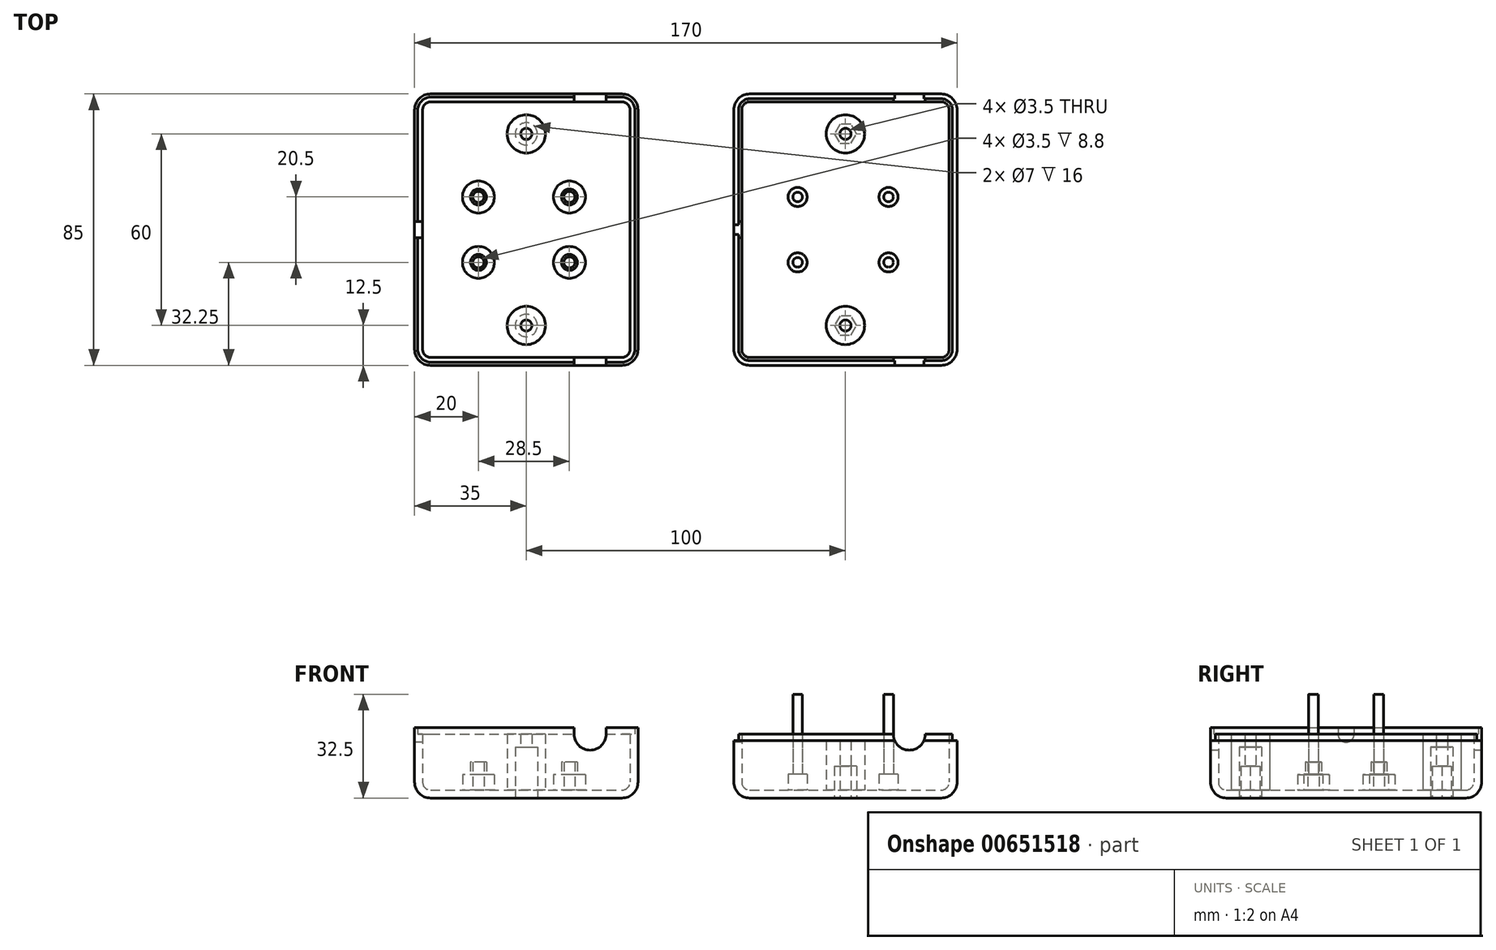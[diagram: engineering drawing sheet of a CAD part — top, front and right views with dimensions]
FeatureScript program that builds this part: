
annotation { "Feature Type Name" : "Feature", "Feature Type Description" : "" }
export const myFeature = defineFeature(function(context is Context, id is Id, definition is map)
    precondition{}
    {
        {
            var Q0;
            Q0=qCreatedBy(makeId("Top.planeOp"),FACE);
            var sketch = newSketch(context, id + "F0", { "sketchPlane" : qUnion([Q0])});
            skLineSegment(sketch, "E0.bottom", {"start": v(0, 0) * mm, "end": v(70, 0) * mm});
            skLineSegment(sketch, "E0.top", {"start": v(0, 85) * mm, "end": v(70, 85) * mm});
            skLineSegment(sketch, "E0.left", {"start": v(0, 0) * mm, "end": v(0, 85) * mm});
            skLineSegment(sketch, "E0.right", {"start": v(70, 0) * mm, "end": v(70, 85) * mm});
            skSolve(sketch);
        }
        {
            var Q0;
            Q0 = qSketchRegion(id + "F0", true);
            extrude(context, id + "F1", {"entities" : qUnion([Q0]), "oppositeDirection" : true, "depth" : 20 * mm, "offsetDistance" : 25 * mm});
        }
        {
            var Q0;
            Q0=makeQuery(id+"F1.opExtrude","CAP_EDGE",EDGE,{"disambiguationData":[OSD([sQuery(id+"F0.wireOp",EDGE,"E0.left")])],"isStart":false});
            var Q1;
            Q1=makeQuery(id+"F1.opExtrude","CAP_FACE",FACE,{"disambiguationData":[OSD([sQuery(id+"F0.wireOp",EDGE,"E0.bottom"),sQuery(id+"F0.wireOp",EDGE,"E0.top"),sQuery(id+"F0.wireOp",EDGE,"E0.left"),sQuery(id+"F0.wireOp",EDGE,"E0.right")])],"isStart":false});
            var Q2;
            Q2=makeQuery(id+"F1.opExtrude","SWEPT_EDGE",EDGE,{"disambiguationData":[OSD([sQuery(id+"F0.wireOp",EDGE,"E0.bottom"),sQuery(id+"F0.wireOp",EDGE,"E0.right")])]});
            var Q3;
            Q3=makeQuery(id+"F1.opExtrude","SWEPT_EDGE",EDGE,{"disambiguationData":[OSD([sQuery(id+"F0.wireOp",EDGE,"E0.bottom"),sQuery(id+"F0.wireOp",EDGE,"E0.left")])]});
            var Q4;
            Q4=makeQuery(id+"F1.opExtrude","SWEPT_EDGE",EDGE,{"disambiguationData":[OSD([sQuery(id+"F0.wireOp",EDGE,"E0.top"),sQuery(id+"F0.wireOp",EDGE,"E0.left")])]});
            var Q5;
            Q5=makeQuery(id+"F1.opExtrude","SWEPT_EDGE",EDGE,{"disambiguationData":[OSD([sQuery(id+"F0.wireOp",EDGE,"E0.top"),sQuery(id+"F0.wireOp",EDGE,"E0.right")])]});
            fillet(context, id + "F2", {"entities" : qUnion([Q0, Q1, Q2, Q3, Q4, Q5]), "radius" : 5 * mm, "tangentPropagation" : true, "allowEdgeOverflow" : false});
        }
        {
            var Q0;
            Q0=makeQuery(id+"F1.opExtrude","CAP_FACE",FACE,{"disambiguationData":[OSD([sQuery(id+"F0.wireOp",EDGE,"E0.bottom"),sQuery(id+"F0.wireOp",EDGE,"E0.top"),sQuery(id+"F0.wireOp",EDGE,"E0.left"),sQuery(id+"F0.wireOp",EDGE,"E0.right")])],"isStart":true});
            shell(context, id + "F3", {"entities" : qUnion([Q0]), "thickness" : 2.5 * mm});
        }
        {
            var Q0;
            Q0=makeQuery(id+"F1.opExtrude","SWEPT_FACE",FACE,{"disambiguationData":[OSD([sQuery(id+"F0.wireOp",EDGE,"E0.left")])]});
            var sketch = newSketch(context, id + "F4", { "sketchPlane" : qUnion([Q0])});
            skCircle(sketch, "E1", {"center": v(-42.5, 0) * mm, "radius": 2.5 * mm});
            skSolve(sketch);
        }
        {
            var Q0;
            Q0 = qSketchRegion(id + "F4", true);
            extrude(context, id + "F5", {"entities" : qUnion([Q0]), "operationType" : NewBodyOperationType.REMOVE, "endBound" : BoundingType.UP_TO_NEXT, "oppositeDirection" : true, "depth" : 25 * mm, "offsetDistance" : 25 * mm});
        }
        {
            var Q0;
            Q0=makeQuery(id+"F1.opExtrude","SWEPT_FACE",FACE,{"disambiguationData":[OSD([sQuery(id+"F0.wireOp",EDGE,"E0.bottom")])]});
            var sketch = newSketch(context, id + "F6", { "sketchPlane" : qUnion([Q0])});
            skCircle(sketch, "E2", {"center": v(55, 0) * mm, "radius": 5 * mm});
            skSolve(sketch);
        }
        {
            var Q0;
            Q0 = qSketchRegion(id + "F6", true);
            extrude(context, id + "F7", {"entities" : qUnion([Q0]), "operationType" : NewBodyOperationType.REMOVE, "endBound" : BoundingType.THROUGH_ALL, "oppositeDirection" : true, "depth" : 25 * mm, "offsetDistance" : 25 * mm});
        }
        {
            var Q0;
            Q0=makeQuery(id+"F3.opShell","OFFSET_FACE",FACE,{"disambiguationData":[OSD([sQuery(id+"F0.wireOp",EDGE,"E0.bottom"),sQuery(id+"F0.wireOp",EDGE,"E0.top"),sQuery(id+"F0.wireOp",EDGE,"E0.left"),sQuery(id+"F0.wireOp",EDGE,"E0.right")])]});
            var sketch = newSketch(context, id + "F8", { "sketchPlane" : qUnion([Q0])});
            skLineSegment(sketch, "E3", {"start": v(5, 42.5) * mm, "end": v(65, 42.5) * mm, "construction": true});
            skLineSegment(sketch, "E4", {"start": v(35, 80) * mm, "end": v(35, 5) * mm, "construction": true});
            skLineSegment(sketch, "E5.bottom", {"start": v(20, 52.75) * mm, "end": v(48.5, 52.75) * mm, "construction": true});
            skLineSegment(sketch, "E5.top", {"start": v(20, 32.25) * mm, "end": v(48.5, 32.25) * mm, "construction": true});
            skLineSegment(sketch, "E5.left", {"start": v(20, 52.75) * mm, "end": v(20, 32.25) * mm, "construction": true});
            skLineSegment(sketch, "E5.right", {"start": v(48.5, 52.75) * mm, "end": v(48.5, 32.25) * mm, "construction": true});
            skSolve(sketch);
        }
        {
            var Q0;
            Q0=makeQuery(id+"F1.opExtrude","SWEPT_BODY",BODY,{"disambiguationData":[OSD([sQuery(id+"F0.wireOp",EDGE,"E0.bottom"),sQuery(id+"F0.wireOp",EDGE,"E0.top"),sQuery(id+"F0.wireOp",EDGE,"E0.left"),sQuery(id+"F0.wireOp",EDGE,"E0.right")])]});
            transform(context, id + "F9", {"entities" : qUnion([Q0]), "transformType" : TransformType.TRANSLATION_3D, "dx" : 100 * mm, "dy" : 0 * mm, "dz" : 0 * mm, "makeCopy" : true});
        }
        {
            var Q0;
            Q0=makeQuery(id+"F9.opPattern","COPY",FACE,{"derivedFrom":makeQuery(id+"F3.opShell","OFFSET_FACE",FACE,{"disambiguationData":[OSD([sQuery(id+"F0.wireOp",EDGE,"E0.bottom"),sQuery(id+"F0.wireOp",EDGE,"E0.top"),sQuery(id+"F0.wireOp",EDGE,"E0.left"),sQuery(id+"F0.wireOp",EDGE,"E0.right")])]}),"instanceName":"1"});
            var sketch = newSketch(context, id + "F10", { "sketchPlane" : qUnion([Q0])});
            skLineSegment(sketch, "E6", {"start": v(105, 42.5) * mm, "end": v(165, 42.5) * mm, "construction": true});
            skLineSegment(sketch, "E7", {"start": v(135, 80) * mm, "end": v(135, 5) * mm, "construction": true});
            skLineSegment(sketch, "E8.bottom", {"start": v(120, 52.75) * mm, "end": v(148.5, 52.75) * mm, "construction": true});
            skLineSegment(sketch, "E8.top", {"start": v(120, 32.25) * mm, "end": v(148.5, 32.25) * mm, "construction": true});
            skLineSegment(sketch, "E8.left", {"start": v(120, 52.75) * mm, "end": v(120, 32.25) * mm, "construction": true});
            skLineSegment(sketch, "E8.right", {"start": v(148.5, 52.75) * mm, "end": v(148.5, 32.25) * mm, "construction": true});
            skSolve(sketch);
        }
        {
            var Q0;
            {var subQ0=sQuery(id+"F0.wireOp",EDGE,"E0.right");var subQ1=sQuery(id+"F0.wireOp",EDGE,"E0.left");var subQ2=sQuery(id+"F0.wireOp",EDGE,"E0.top");var subQ3=sQuery(id+"F0.wireOp",EDGE,"E0.bottom");var subQ4=makeQuery(id+"F1.opExtrude","CAP_FACE",FACE,{"disambiguationData":[OSD([subQ3,subQ2,subQ1,subQ0])],"isStart":false});Q0=makeQuery(id+"F8.imprint","IMPRINT",FACE,{"disambiguationData":[TD([[makeQuery(id+"F8.imprint","IMPRINT",EDGE,{"derivedFrom":makeQuery(id+"F3.opShell","OFFSET_EDGE",EDGE,{"disambiguationData":[OSD([subQ3,subQ2,subQ1,subQ0]),TDD([makeQuery(id+"F2.opFillet","BLEND_EDGE",EDGE,{"blendedFrom":[makeQuery(id+"F1.opExtrude","CAP_EDGE",EDGE,{"disambiguationData":[OSD([subQ3])],"isStart":false}),subQ4],"blendedInto":[subQ4]})])]})}),-1.0]])]});}
            var sketch = newSketch(context, id + "F11", { "sketchPlane" : qUnion([Q0])});
            skCircle(sketch, "E9", {"center": v(20, 52.75) * mm, "radius": 5 * mm});
            skCircle(sketch, "E10", {"center": v(48.5, 52.75) * mm, "radius": 5 * mm});
            skCircle(sketch, "E11", {"center": v(48.5, 32.25) * mm, "radius": 5 * mm});
            skCircle(sketch, "E12", {"center": v(20, 32.25) * mm, "radius": 5 * mm});
            skCircle(sketch, "E13", {"center": v(20, 52.75) * mm, "radius": 1.75 * mm});
            skCircle(sketch, "E14", {"center": v(48.5, 52.75) * mm, "radius": 1.75 * mm});
            skCircle(sketch, "E15", {"center": v(48.5, 32.25) * mm, "radius": 1.75 * mm});
            skCircle(sketch, "E16", {"center": v(20, 32.25) * mm, "radius": 1.75 * mm});
            skSolve(sketch);
        }
        {
            var Q0;
            Q0 = qSketchRegion(id + "F11", true);
            extrude(context, id + "F12", {"entities" : qUnion([Q0]), "operationType" : NewBodyOperationType.ADD, "depth" : 4.8 * mm, "offsetDistance" : 25 * mm});
        }
        {
            var Q0;
            Q0=makeQuery(id+"F12.opExtrude","CAP_FACE",FACE,{"disambiguationData":[OSD([sQuery(id+"F11.wireOp",EDGE,"E9"),sQuery(id+"F11.wireOp",EDGE,"E13")])],"isStart":false});
            var sketch = newSketch(context, id + "F13", { "sketchPlane" : qUnion([Q0])});
            skCircle(sketch, "E17", {"center": v(20, 52.75) * mm, "radius": 2.5 * mm});
            skCircle(sketch, "E18", {"center": v(20, 32.25) * mm, "radius": 2.5 * mm});
            skCircle(sketch, "E19", {"center": v(48.5, 32.25) * mm, "radius": 2.5 * mm});
            skCircle(sketch, "E20", {"center": v(48.5, 52.75) * mm, "radius": 2.5 * mm});
            skCircle(sketch, "E21.0", {"center": v(20, 52.75) * mm, "radius": 1.75 * mm});
            skCircle(sketch, "E22.0", {"center": v(48.5, 52.75) * mm, "radius": 1.75 * mm});
            skCircle(sketch, "E23.0", {"center": v(48.5, 32.25) * mm, "radius": 1.75 * mm});
            skCircle(sketch, "E24.0", {"center": v(20, 32.25) * mm, "radius": 1.75 * mm});
            skSolve(sketch);
        }
        {
            var Q0;
            Q0 = qSketchRegion(id + "F13", true);
            extrude(context, id + "F14", {"entities" : qUnion([Q0]), "operationType" : NewBodyOperationType.ADD, "depth" : 4 * mm, "offsetDistance" : 25 * mm});
        }
        {
            var Q0;
            {var subQ0=sQuery(id+"F0.wireOp",EDGE,"E0.right");var subQ1=sQuery(id+"F0.wireOp",EDGE,"E0.left");var subQ2=sQuery(id+"F0.wireOp",EDGE,"E0.top");var subQ3=sQuery(id+"F0.wireOp",EDGE,"E0.bottom");var subQ4=makeQuery(id+"F1.opExtrude","CAP_FACE",FACE,{"disambiguationData":[OSD([subQ3,subQ2,subQ1,subQ0])],"isStart":false});Q0=makeQuery(id+"F10.imprint","IMPRINT",FACE,{"disambiguationData":[TD([[makeQuery(id+"F10.imprint","IMPRINT",EDGE,{"derivedFrom":makeQuery(id+"F9.opPattern","COPY",EDGE,{"derivedFrom":makeQuery(id+"F3.opShell","OFFSET_EDGE",EDGE,{"disambiguationData":[OSD([subQ3,subQ2,subQ1,subQ0]),TDD([makeQuery(id+"F2.opFillet","BLEND_EDGE",EDGE,{"blendedFrom":[makeQuery(id+"F1.opExtrude","CAP_EDGE",EDGE,{"disambiguationData":[OSD([subQ3])],"isStart":false}),subQ4],"blendedInto":[subQ4]})])]}),"instanceName":"1"})}),-1.0]])]});}
            var sketch = newSketch(context, id + "F15", { "sketchPlane" : qUnion([Q0])});
            skCircle(sketch, "E25", {"center": v(120, 52.75) * mm, "radius": 1.5 * mm});
            skCircle(sketch, "E26", {"center": v(148.5, 52.75) * mm, "radius": 1.5 * mm});
            skCircle(sketch, "E27", {"center": v(148.5, 32.25) * mm, "radius": 1.5 * mm});
            skCircle(sketch, "E28", {"center": v(120, 32.25) * mm, "radius": 1.5 * mm});
            skSolve(sketch);
        }
        {
            var Q0;
            Q0 = qSketchRegion(id + "F15", true);
            extrude(context, id + "F16", {"entities" : qUnion([Q0]), "operationType" : NewBodyOperationType.ADD, "depth" : 30 * mm, "offsetDistance" : 25 * mm});
        }
        {
            var Q0;
            {var subQ0=sQuery(id+"F0.wireOp",EDGE,"E0.right");var subQ1=sQuery(id+"F0.wireOp",EDGE,"E0.left");var subQ2=sQuery(id+"F0.wireOp",EDGE,"E0.top");var subQ3=sQuery(id+"F0.wireOp",EDGE,"E0.bottom");var subQ4=makeQuery(id+"F1.opExtrude","CAP_FACE",FACE,{"disambiguationData":[OSD([subQ3,subQ2,subQ1,subQ0])],"isStart":false});Q0=makeQuery(id+"F10.imprint","IMPRINT",FACE,{"disambiguationData":[TD([[makeQuery(id+"F10.imprint","IMPRINT",EDGE,{"derivedFrom":makeQuery(id+"F9.opPattern","COPY",EDGE,{"derivedFrom":makeQuery(id+"F3.opShell","OFFSET_EDGE",EDGE,{"disambiguationData":[OSD([subQ3,subQ2,subQ1,subQ0]),TDD([makeQuery(id+"F2.opFillet","BLEND_EDGE",EDGE,{"blendedFrom":[makeQuery(id+"F1.opExtrude","CAP_EDGE",EDGE,{"disambiguationData":[OSD([subQ3])],"isStart":false}),subQ4],"blendedInto":[subQ4]})])]}),"instanceName":"1"})}),-1.0]])]});}
            var sketch = newSketch(context, id + "F17", { "sketchPlane" : qUnion([Q0])});
            skCircle(sketch, "E29", {"center": v(148.5, 52.75) * mm, "radius": 3 * mm});
            skCircle(sketch, "E30", {"center": v(148.5, 32.25) * mm, "radius": 3 * mm});
            skCircle(sketch, "E31", {"center": v(120, 32.25) * mm, "radius": 3 * mm});
            skCircle(sketch, "E32", {"center": v(120, 52.75) * mm, "radius": 3 * mm});
            skCircle(sketch, "E33.0", {"center": v(148.5, 52.75) * mm, "radius": 1.5 * mm});
            skCircle(sketch, "E34.0", {"center": v(120, 52.75) * mm, "radius": 1.5 * mm});
            skCircle(sketch, "E35.0", {"center": v(120, 32.25) * mm, "radius": 1.5 * mm});
            skCircle(sketch, "E36.0", {"center": v(148.5, 32.25) * mm, "radius": 1.5 * mm});
            skSolve(sketch);
        }
        {
            var Q0;
            Q0 = qSketchRegion(id + "F17", true);
            extrude(context, id + "F18", {"entities" : qUnion([Q0]), "operationType" : NewBodyOperationType.ADD, "depth" : 5 * mm, "offsetDistance" : 25 * mm});
        }
        {
            var Q0;
            {var subQ0=sQuery(id+"F0.wireOp",EDGE,"E0.left");var subQ1=sQuery(id+"F0.wireOp",EDGE,"E0.top");var subQ2=makeQuery(id+"F2.opFillet","BLEND_FACE",FACE,{"disambiguationData":[OSD([subQ1,subQ0]),TDD([makeQuery(id+"F1.opExtrude","SWEPT_EDGE",EDGE,{"disambiguationData":[OSD([subQ1,subQ0])]})])]});Q0=makeQuery(id+"F7.boolean.opBoolean","SPLIT",FACE,{"disambiguationData":[TD([subQ2])],"derivedFrom":makeQuery(id+"F1.opExtrude","CAP_FACE",FACE,{"disambiguationData":[OSD([sQuery(id+"F0.wireOp",EDGE,"E0.bottom"),subQ1,subQ0,sQuery(id+"F0.wireOp",EDGE,"E0.right")])],"isStart":true})});}
            var sketch = newSketch(context, id + "F19", { "sketchPlane" : qUnion([Q0])});
            skLineSegment(sketch, "E37.0", {"start": v(1, 45) * mm, "end": v(1, 80) * mm});
            skArc(sketch, "E37.1", {"start": v(5, 84) * mm, "mid": v(2.17, 82.83) * mm, "end": v(1, 80) * mm});
            skLineSegment(sketch, "E37.2", {"start": v(5, 84) * mm, "end": v(50, 84) * mm});
            skLineSegment(sketch, "E38.0", {"start": v(60, 84) * mm, "end": v(65, 84) * mm});
            skLineSegment(sketch, "E38.1", {"start": v(60, 1) * mm, "end": v(65, 1) * mm});
            skArc(sketch, "E38.2", {"start": v(65, 1) * mm, "mid": v(67.83, 2.17) * mm, "end": v(69, 5) * mm});
            skLineSegment(sketch, "E38.3", {"start": v(69, 5) * mm, "end": v(69, 80) * mm});
            skArc(sketch, "E38.4", {"start": v(69, 80) * mm, "mid": v(67.83, 82.83) * mm, "end": v(65, 84) * mm});
            skLineSegment(sketch, "E39.0", {"start": v(5, 1) * mm, "end": v(50, 1) * mm});
            skArc(sketch, "E39.1", {"start": v(1, 5) * mm, "mid": v(2.17, 2.17) * mm, "end": v(5, 1) * mm});
            skLineSegment(sketch, "E39.2", {"start": v(1, 5) * mm, "end": v(1, 40) * mm});
            skLineSegment(sketch, "E40.0", {"start": v(0, 45) * mm, "end": v(0, 80) * mm});
            skArc(sketch, "E41.0", {"start": v(5, 85) * mm, "mid": v(1.46, 83.54) * mm, "end": v(0, 80) * mm});
            skLineSegment(sketch, "E42.0", {"start": v(5, 85) * mm, "end": v(50, 85) * mm});
            skLineSegment(sketch, "E43.0", {"start": v(60, 85) * mm, "end": v(65, 85) * mm});
            skArc(sketch, "E44.0", {"start": v(70, 80) * mm, "mid": v(68.54, 83.54) * mm, "end": v(65, 85) * mm});
            skLineSegment(sketch, "E45.0", {"start": v(70, 5) * mm, "end": v(70, 80) * mm});
            skLineSegment(sketch, "E46.0", {"start": v(60, 0) * mm, "end": v(65, 0) * mm});
            skArc(sketch, "E47.0", {"start": v(65, 0) * mm, "mid": v(68.54, 1.46) * mm, "end": v(70, 5) * mm});
            skLineSegment(sketch, "E48.0", {"start": v(5, 0) * mm, "end": v(50, 0) * mm});
            skLineSegment(sketch, "E49.0", {"start": v(0, 5) * mm, "end": v(0, 40) * mm});
            skArc(sketch, "E50.0", {"start": v(0, 5) * mm, "mid": v(1.46, 1.46) * mm, "end": v(5, 0) * mm});
            skLineSegment(sketch, "E51", {"start": v(50, 1) * mm, "end": v(50, 0) * mm});
            skLineSegment(sketch, "E52", {"start": v(60, 1) * mm, "end": v(60, 0) * mm});
            skLineSegment(sketch, "E53", {"start": v(0, 45) * mm, "end": v(1, 45) * mm});
            skLineSegment(sketch, "E54", {"start": v(0, 40) * mm, "end": v(1, 40) * mm});
            skLineSegment(sketch, "E55", {"start": v(60, 85) * mm, "end": v(60, 84) * mm});
            skLineSegment(sketch, "E56", {"start": v(50, 85) * mm, "end": v(50, 84) * mm});
            skSolve(sketch);
        }
        {
            var Q0;
            Q0 = qSketchRegion(id + "F19", true);
            extrude(context, id + "F20", {"entities" : qUnion([Q0]), "operationType" : NewBodyOperationType.ADD, "depth" : 2 * mm, "offsetDistance" : 25 * mm});
        }
        {
            var Q0;
            {var subQ0=sQuery(id+"F0.wireOp",EDGE,"E0.left");var subQ1=sQuery(id+"F0.wireOp",EDGE,"E0.top");var subQ2=makeQuery(id+"F2.opFillet","BLEND_FACE",FACE,{"disambiguationData":[OSD([subQ1,subQ0]),TDD([makeQuery(id+"F1.opExtrude","SWEPT_EDGE",EDGE,{"disambiguationData":[OSD([subQ1,subQ0])]})])]});Q0=makeQuery(id+"F9.opPattern","COPY",FACE,{"derivedFrom":makeQuery(id+"F7.boolean.opBoolean","SPLIT",FACE,{"disambiguationData":[TD([subQ2])],"derivedFrom":makeQuery(id+"F1.opExtrude","CAP_FACE",FACE,{"disambiguationData":[OSD([sQuery(id+"F0.wireOp",EDGE,"E0.bottom"),subQ1,subQ0,sQuery(id+"F0.wireOp",EDGE,"E0.right")])],"isStart":true})}),"instanceName":"1"});}
            var sketch = newSketch(context, id + "F21", { "sketchPlane" : qUnion([Q0])});
            skLineSegment(sketch, "E57.0", {"start": v(101.5, 45) * mm, "end": v(101.5, 80) * mm});
            skArc(sketch, "E57.1", {"start": v(105, 83.5) * mm, "mid": v(102.53, 82.47) * mm, "end": v(101.5, 80) * mm});
            skLineSegment(sketch, "E57.2", {"start": v(105, 83.5) * mm, "end": v(150, 83.5) * mm});
            skLineSegment(sketch, "E58.0", {"start": v(160, 83.5) * mm, "end": v(165, 83.5) * mm});
            skLineSegment(sketch, "E58.1", {"start": v(160, 1.5) * mm, "end": v(165, 1.5) * mm});
            skArc(sketch, "E58.2", {"start": v(165, 1.5) * mm, "mid": v(167.47, 2.53) * mm, "end": v(168.5, 5) * mm});
            skLineSegment(sketch, "E58.3", {"start": v(168.5, 5) * mm, "end": v(168.5, 80) * mm});
            skArc(sketch, "E58.4", {"start": v(168.5, 80) * mm, "mid": v(167.47, 82.47) * mm, "end": v(165, 83.5) * mm});
            skLineSegment(sketch, "E59.0", {"start": v(105, 1.5) * mm, "end": v(150, 1.5) * mm});
            skArc(sketch, "E59.1", {"start": v(101.5, 5) * mm, "mid": v(102.53, 2.53) * mm, "end": v(105, 1.5) * mm});
            skLineSegment(sketch, "E59.2", {"start": v(101.5, 5) * mm, "end": v(101.5, 40) * mm});
            skLineSegment(sketch, "E60.0", {"start": v(100, 45) * mm, "end": v(100, 80) * mm});
            skArc(sketch, "E61.0", {"start": v(105, 85) * mm, "mid": v(101.46, 83.54) * mm, "end": v(100, 80) * mm});
            skLineSegment(sketch, "E62.0", {"start": v(105, 85) * mm, "end": v(150, 85) * mm});
            skLineSegment(sketch, "E63.0", {"start": v(160, 85) * mm, "end": v(165, 85) * mm});
            skArc(sketch, "E64.0", {"start": v(170, 80) * mm, "mid": v(168.54, 83.54) * mm, "end": v(165, 85) * mm});
            skLineSegment(sketch, "E65.0", {"start": v(170, 5) * mm, "end": v(170, 80) * mm});
            skArc(sketch, "E66.0", {"start": v(165, 0) * mm, "mid": v(168.54, 1.46) * mm, "end": v(170, 5) * mm});
            skLineSegment(sketch, "E67.0", {"start": v(160, 0) * mm, "end": v(165, 0) * mm});
            skLineSegment(sketch, "E68.0", {"start": v(105, 0) * mm, "end": v(150, 0) * mm});
            skArc(sketch, "E69.0", {"start": v(100, 5) * mm, "mid": v(101.46, 1.46) * mm, "end": v(105, 0) * mm});
            skLineSegment(sketch, "E70.0", {"start": v(100, 5) * mm, "end": v(100, 40) * mm});
            skLineSegment(sketch, "E71", {"start": v(160, 83.5) * mm, "end": v(150, 83.5) * mm});
            skLineSegment(sketch, "E72", {"start": v(150, 85) * mm, "end": v(160, 85) * mm});
            skLineSegment(sketch, "E73", {"start": v(100, 40) * mm, "end": v(100, 45) * mm});
            skLineSegment(sketch, "E74", {"start": v(101.5, 45) * mm, "end": v(101.5, 40) * mm});
            skLineSegment(sketch, "E75", {"start": v(160, 0) * mm, "end": v(150, 0) * mm});
            skLineSegment(sketch, "E76", {"start": v(150, 1.5) * mm, "end": v(160, 1.5) * mm});
            skSolve(sketch);
        }
        {
            var Q0;
            Q0 = qSketchRegion(id + "F21", true);
            extrude(context, id + "F22", {"entities" : qUnion([Q0]), "operationType" : NewBodyOperationType.REMOVE, "oppositeDirection" : true, "depth" : 2 * mm, "offsetDistance" : 25 * mm});
        }
        {
            var Q0;
            {var subQ0=sQuery(id+"F0.wireOp",EDGE,"E0.left");var subQ1=sQuery(id+"F0.wireOp",EDGE,"E0.top");var subQ2=sQuery(id+"F0.wireOp",EDGE,"E0.bottom");var subQ3=sQuery(id+"F0.wireOp",EDGE,"E0.right");Q0=makeQuery(id+"F12.boolean.opBoolean","SPLIT",FACE,{"disambiguationData":[TD([makeQuery(id+"F12.opExtrude","SWEPT_FACE",FACE,{"disambiguationData":[OSD([sQuery(id+"F11.wireOp",EDGE,"E9")])]})])],"derivedFrom":makeQuery(id+"F3.opShell","OFFSET_FACE",FACE,{"disambiguationData":[OSD([subQ2,subQ1,subQ0,subQ3])]})});}
            var sketch = newSketch(context, id + "F23", { "sketchPlane" : qUnion([Q0])});
            skLineSegment(sketch, "E77", {"start": v(35, 80) * mm, "end": v(35, 5) * mm, "construction": true});
            skLineSegment(sketch, "E78", {"start": v(5, 42.5) * mm, "end": v(65, 42.5) * mm, "construction": true});
            skCircle(sketch, "E79", {"center": v(35, 72.5) * mm, "radius": 6 * mm});
            skCircle(sketch, "E80", {"center": v(35, 12.5) * mm, "radius": 6 * mm});
            skSolve(sketch);
        }
        {
            var Q0;
            Q0 = qSketchRegion(id + "F23", true);
            var Q1;
            {var subQ0=sQuery(id+"F0.wireOp",EDGE,"E0.left");var subQ1=sQuery(id+"F0.wireOp",EDGE,"E0.top");var subQ2=makeQuery(id+"F2.opFillet","BLEND_FACE",FACE,{"disambiguationData":[OSD([subQ1,subQ0]),TDD([makeQuery(id+"F1.opExtrude","SWEPT_EDGE",EDGE,{"disambiguationData":[OSD([subQ1,subQ0])]})])]});Q1=makeQuery(id+"F7.boolean.opBoolean","SPLIT",FACE,{"disambiguationData":[TD([subQ2])],"derivedFrom":makeQuery(id+"F1.opExtrude","CAP_FACE",FACE,{"disambiguationData":[OSD([sQuery(id+"F0.wireOp",EDGE,"E0.bottom"),subQ1,subQ0,sQuery(id+"F0.wireOp",EDGE,"E0.right")])],"isStart":true})});}
            extrude(context, id + "F24", {"entities" : qUnion([Q0]), "operationType" : NewBodyOperationType.ADD, "endBound" : BoundingType.UP_TO_SURFACE, "depth" : 25 * mm, "endBoundEntityFace" : qUnion([Q1]), "offsetDistance" : 25 * mm});
        }
        {
            var Q0;
            Q0=makeQuery(id+"F9.opPattern","COPY",FACE,{"derivedFrom":makeQuery(id+"F3.opShell","OFFSET_FACE",FACE,{"disambiguationData":[OSD([sQuery(id+"F0.wireOp",EDGE,"E0.bottom"),sQuery(id+"F0.wireOp",EDGE,"E0.top"),sQuery(id+"F0.wireOp",EDGE,"E0.left"),sQuery(id+"F0.wireOp",EDGE,"E0.right")])]}),"instanceName":"1"});
            var sketch = newSketch(context, id + "F25", { "sketchPlane" : qUnion([Q0])});
            skLineSegment(sketch, "E81", {"start": v(135, 80) * mm, "end": v(135, 5) * mm, "construction": true});
            skLineSegment(sketch, "E82", {"start": v(105, 42.5) * mm, "end": v(165, 42.5) * mm, "construction": true});
            skCircle(sketch, "E83", {"center": v(135, 72.5) * mm, "radius": 6 * mm});
            skCircle(sketch, "E84", {"center": v(135, 12.5) * mm, "radius": 6 * mm});
            skSolve(sketch);
        }
        {
            var Q0;
            Q0 = qSketchRegion(id + "F25", true);
            var Q1;
            {var subQ4=sQuery(id+"F21.wireOp",EDGE,"E74");var subQ5=sQuery(id+"F21.wireOp",EDGE,"E59.2");var subQ6=sQuery(id+"F21.wireOp",EDGE,"E57.0");var subQ7=sQuery(id+"F21.wireOp",EDGE,"E57.1");var subQ8=sQuery(id+"F21.wireOp",EDGE,"E71");var subQ9=sQuery(id+"F21.wireOp",EDGE,"E58.0");var subQ10=sQuery(id+"F21.wireOp",EDGE,"E57.2");Q1=makeQuery(id+"F22.boolean.opBoolean","COPY",FACE,{"disambiguationData":[TD([makeQuery(id+"F22.opExtrude","SWEPT_FACE",FACE,{"disambiguationData":[OSD([subQ7])]})])],"derivedFrom":makeQuery(id+"F22.opExtrude","CAP_FACE",FACE,{"disambiguationData":[OSD([subQ6,subQ7,subQ10,subQ9,sQuery(id+"F21.wireOp",EDGE,"E58.1"),sQuery(id+"F21.wireOp",EDGE,"E58.2"),sQuery(id+"F21.wireOp",EDGE,"E58.3"),sQuery(id+"F21.wireOp",EDGE,"E58.4"),sQuery(id+"F21.wireOp",EDGE,"E59.0"),sQuery(id+"F21.wireOp",EDGE,"E59.1"),subQ5,sQuery(id+"F21.wireOp",EDGE,"E60.0"),sQuery(id+"F21.wireOp",EDGE,"E61.0"),sQuery(id+"F21.wireOp",EDGE,"E62.0"),sQuery(id+"F21.wireOp",EDGE,"E63.0"),sQuery(id+"F21.wireOp",EDGE,"E64.0"),sQuery(id+"F21.wireOp",EDGE,"E65.0"),sQuery(id+"F21.wireOp",EDGE,"E66.0"),sQuery(id+"F21.wireOp",EDGE,"E67.0"),sQuery(id+"F21.wireOp",EDGE,"E68.0"),sQuery(id+"F21.wireOp",EDGE,"E69.0"),sQuery(id+"F21.wireOp",EDGE,"E70.0"),subQ8,sQuery(id+"F21.wireOp",EDGE,"E72"),sQuery(id+"F21.wireOp",EDGE,"E73"),subQ4,sQuery(id+"F21.wireOp",EDGE,"E75"),sQuery(id+"F21.wireOp",EDGE,"E76")])],"isStart":false})});}
            extrude(context, id + "F26", {"entities" : qUnion([Q0]), "operationType" : NewBodyOperationType.ADD, "endBound" : BoundingType.UP_TO_SURFACE, "depth" : 25 * mm, "endBoundEntityFace" : qUnion([Q1]), "offsetDistance" : 25 * mm});
        }
        {
            var Q0;
            Q0=makeQuery(id+"F1.opExtrude","CAP_FACE",FACE,{"disambiguationData":[OSD([sQuery(id+"F0.wireOp",EDGE,"E0.bottom"),sQuery(id+"F0.wireOp",EDGE,"E0.top"),sQuery(id+"F0.wireOp",EDGE,"E0.left"),sQuery(id+"F0.wireOp",EDGE,"E0.right")])],"isStart":false});
            var sketch = newSketch(context, id + "F27", { "sketchPlane" : qUnion([Q0])});
            skCircle(sketch, "E85", {"center": v(35, -12.5) * mm, "radius": 3.5 * mm});
            skCircle(sketch, "E86", {"center": v(35, -72.5) * mm, "radius": 3.5 * mm});
            skSolve(sketch);
        }
        {
            var Q0;
            Q0 = qSketchRegion(id + "F27", true);
            extrude(context, id + "F28", {"entities" : qUnion([Q0]), "operationType" : NewBodyOperationType.REMOVE, "oppositeDirection" : true, "depth" : 16 * mm, "offsetDistance" : 25 * mm});
        }
        {
            var Q0;
            Q0=makeQuery(id+"F1.opExtrude","CAP_FACE",FACE,{"disambiguationData":[OSD([sQuery(id+"F0.wireOp",EDGE,"E0.bottom"),sQuery(id+"F0.wireOp",EDGE,"E0.top"),sQuery(id+"F0.wireOp",EDGE,"E0.left"),sQuery(id+"F0.wireOp",EDGE,"E0.right")])],"isStart":false});
            var sketch = newSketch(context, id + "F29", { "sketchPlane" : qUnion([Q0])});
            skCircle(sketch, "E87", {"center": v(35, -12.5) * mm, "radius": 1.75 * mm});
            skCircle(sketch, "E88", {"center": v(35, -72.5) * mm, "radius": 1.75 * mm});
            skSolve(sketch);
        }
        {
            var Q0;
            Q0 = qSketchRegion(id + "F29", true);
            extrude(context, id + "F30", {"entities" : qUnion([Q0]), "operationType" : NewBodyOperationType.REMOVE, "endBound" : BoundingType.THROUGH_ALL, "oppositeDirection" : true, "depth" : 25 * mm, "offsetDistance" : 25 * mm});
        }
        {
            var Q0;
            Q0=makeQuery(id+"F9.opPattern","COPY",FACE,{"derivedFrom":makeQuery(id+"F1.opExtrude","CAP_FACE",FACE,{"disambiguationData":[OSD([sQuery(id+"F0.wireOp",EDGE,"E0.bottom"),sQuery(id+"F0.wireOp",EDGE,"E0.top"),sQuery(id+"F0.wireOp",EDGE,"E0.left"),sQuery(id+"F0.wireOp",EDGE,"E0.right")])],"isStart":false}),"instanceName":"1"});
            var sketch = newSketch(context, id + "F31", { "sketchPlane" : qUnion([Q0])});
            skCircle(sketch, "E89.cCircle", {"center": v(135, -12.5) * mm, "radius": 3 * mm, "construction": true});
            skLineSegment(sketch, "E89.0", {"start": v(136.73, -15.5) * mm, "end": v(133.27, -15.5) * mm});
            skLineSegment(sketch, "E89.1", {"start": v(133.27, -15.5) * mm, "end": v(131.54, -12.5) * mm});
            skLineSegment(sketch, "E89.2", {"start": v(131.54, -12.5) * mm, "end": v(133.27, -9.5) * mm});
            skLineSegment(sketch, "E89.3", {"start": v(133.27, -9.5) * mm, "end": v(136.73, -9.5) * mm});
            skLineSegment(sketch, "E89.4", {"start": v(136.73, -9.5) * mm, "end": v(138.46, -12.5) * mm});
            skLineSegment(sketch, "E89.5", {"start": v(138.46, -12.5) * mm, "end": v(136.73, -15.5) * mm});
            skPoint(sketch, "E89.0.midPoint", {"position": v(135, -15.5) * mm});
            skCircle(sketch, "E90.cCircle", {"center": v(135, -72.5) * mm, "radius": 3 * mm, "construction": true});
            skLineSegment(sketch, "E90.0", {"start": v(136.73, -75.5) * mm, "end": v(133.27, -75.5) * mm});
            skLineSegment(sketch, "E90.1", {"start": v(133.27, -75.5) * mm, "end": v(131.54, -72.5) * mm});
            skLineSegment(sketch, "E90.2", {"start": v(131.54, -72.5) * mm, "end": v(133.27, -69.5) * mm});
            skLineSegment(sketch, "E90.3", {"start": v(133.27, -69.5) * mm, "end": v(136.73, -69.5) * mm});
            skLineSegment(sketch, "E90.4", {"start": v(136.73, -69.5) * mm, "end": v(138.46, -72.5) * mm});
            skLineSegment(sketch, "E90.5", {"start": v(138.46, -72.5) * mm, "end": v(136.73, -75.5) * mm});
            skPoint(sketch, "E90.0.midPoint", {"position": v(135, -75.5) * mm});
            skSolve(sketch);
        }
        {
            var Q0;
            Q0 = qSketchRegion(id + "F31", true);
            extrude(context, id + "F32", {"entities" : qUnion([Q0]), "operationType" : NewBodyOperationType.REMOVE, "oppositeDirection" : true, "depth" : 10 * mm, "offsetDistance" : 25 * mm});
        }
        {
            var Q0;
            Q0=makeQuery(id+"F9.opPattern","COPY",FACE,{"derivedFrom":makeQuery(id+"F1.opExtrude","CAP_FACE",FACE,{"disambiguationData":[OSD([sQuery(id+"F0.wireOp",EDGE,"E0.bottom"),sQuery(id+"F0.wireOp",EDGE,"E0.top"),sQuery(id+"F0.wireOp",EDGE,"E0.left"),sQuery(id+"F0.wireOp",EDGE,"E0.right")])],"isStart":false}),"instanceName":"1"});
            var sketch = newSketch(context, id + "F33", { "sketchPlane" : qUnion([Q0])});
            skCircle(sketch, "E91", {"center": v(135, -12.5) * mm, "radius": 1.75 * mm});
            skCircle(sketch, "E92", {"center": v(135, -72.5) * mm, "radius": 1.75 * mm});
            skSolve(sketch);
        }
        {
            var Q0;
            Q0 = qSketchRegion(id + "F33", true);
            extrude(context, id + "F34", {"entities" : qUnion([Q0]), "operationType" : NewBodyOperationType.REMOVE, "endBound" : BoundingType.THROUGH_ALL, "oppositeDirection" : true, "depth" : 25 * mm, "offsetDistance" : 25 * mm});
        }
    });
